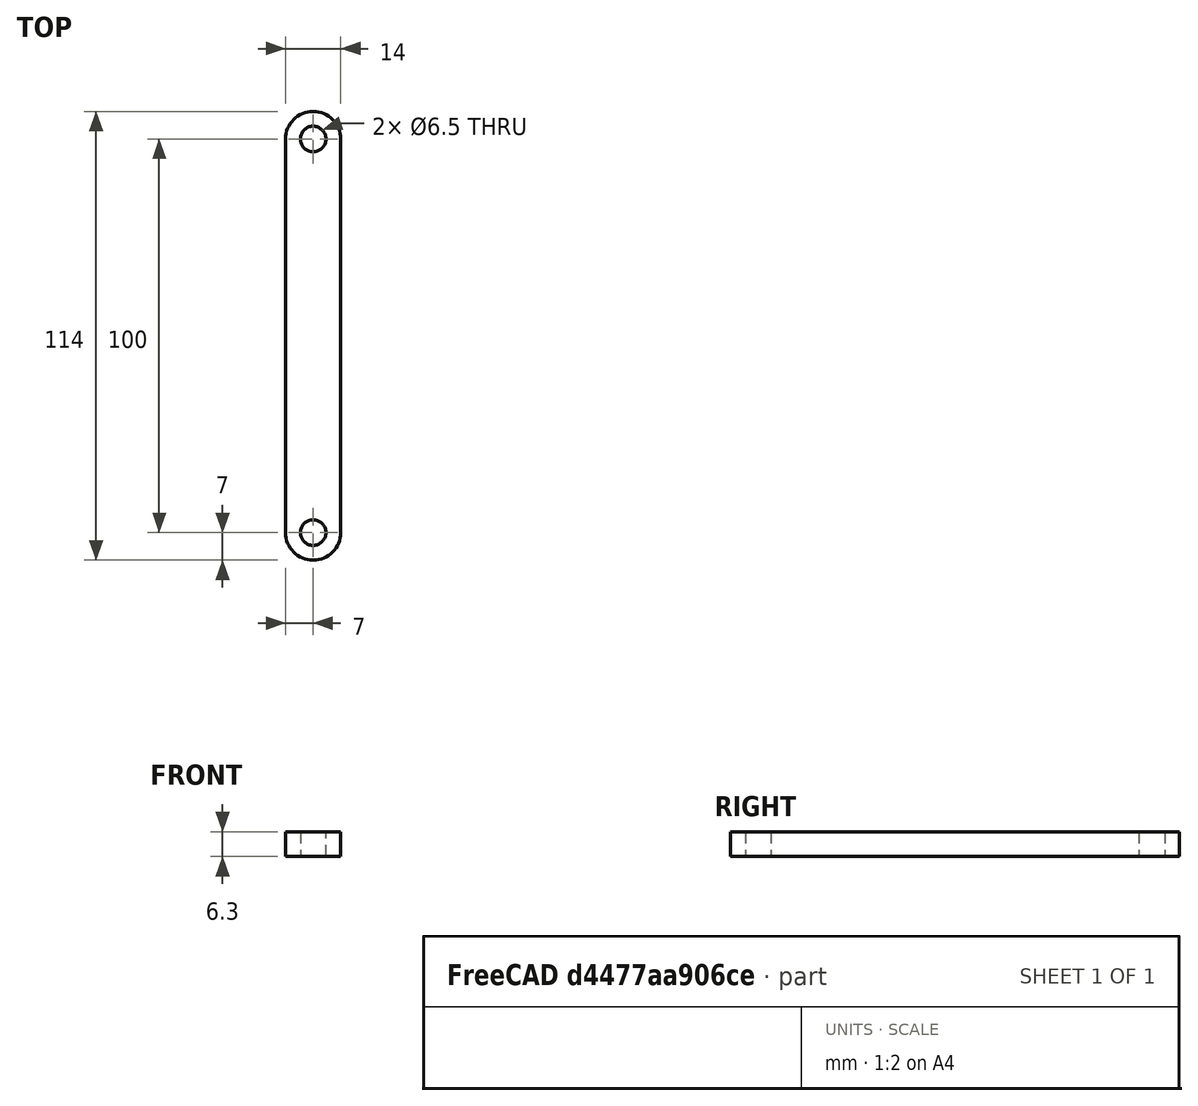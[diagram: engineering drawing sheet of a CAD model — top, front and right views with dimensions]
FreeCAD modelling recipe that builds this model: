
FCSTD DOCUMENT  (FreeCAD 1.2R44800 (Git))
Label: HamSupport
License: All rights reserved
LicenseURL: https://en.wikipedia.org/wiki/All_rights_reserved
objects: App::Point×1, Sketcher::SketchObject×1, PartDesign::Pad×1, PartDesign::Body×1
note: 6 computed .brp shape members not serialized (recipe doc carries the construction recipe); baked Part::Feature solids carry a one-line shape summary decoded from their .brp

FEATURE [App::Point] Origin001
  Role = Origin
FEATURE [Sketcher::SketchObject] Sketch
  ArcFitTolerance = 1e-06
  AttachmentSupport = -> [Origin]
  ExternalTypes = [0]
  FullyConstrained = true
  MakeInternals = false
  MapMode = 5
  sketch-geometry (6):
    g0: Circle CenterX=0 CenterY=0 CenterZ=0 NormalX=0 NormalY=0 NormalZ=1 AngleXU=0 Radius=3.25
    g1: Circle CenterX=0 CenterY=100 CenterZ=0 NormalX=0 NormalY=0 NormalZ=1 AngleXU=0 Radius=3.25
    g2: ArcOfCircle CenterX=0 CenterY=100 CenterZ=0 NormalX=0 NormalY=0 NormalZ=1 AngleXU=0 Radius=7 StartAngle=9e-16 EndAngle=3.14159
    g3: ArcOfCircle CenterX=0 CenterY=0 CenterZ=0 NormalX=0 NormalY=0 NormalZ=1 AngleXU=0 Radius=7 StartAngle=3.14159 EndAngle=6.28319
    g4: LineSegment StartX=7 StartY=100 StartZ=0 EndX=7 EndY=0 EndZ=0
    g5: LineSegment StartX=-7 StartY=100 StartZ=0 EndX=-7 EndY=0 EndZ=0
  constraints (14):
    c: Diameter(g0) = 6.5
    c: Coincident(g0,g-1)
    c: PointOnObject(g1,g-2)
    c: Equal(g1,g0)
    c: DistanceY(g-1,g1) = 100
    c: Tangent(g2,g4) = 1.5708
    c: Tangent(g2,g5) = -1.5708
    c: Tangent(g3,g4) = 1.5708
    c: Tangent(g3,g5) = -1.5708
    c: Equal(g2,g3)
    c: Coincident(g2,g1)
    c: Coincident(g3,g0)
    c: Distance(g0,g3) = 3.75
    c: Distance(g3,g3) = 14
FEATURE [PartDesign::Pad] Pad
  Direction = (0,0,1)
  Length = 6.3
  Length2 = 10
  Profile = -> Sketch
  ReferenceAxis = -> Sketch [N_Axis]
  Refine = true
  SideType = 0
  Suppressed = false
  Type = 0
  Type2 = 0
FEATURE [PartDesign::Body] Body
  AllowCompound = false
  Group = -> [Sketch,Pad]
  Origin = -> Origin
  Tip = -> Pad
